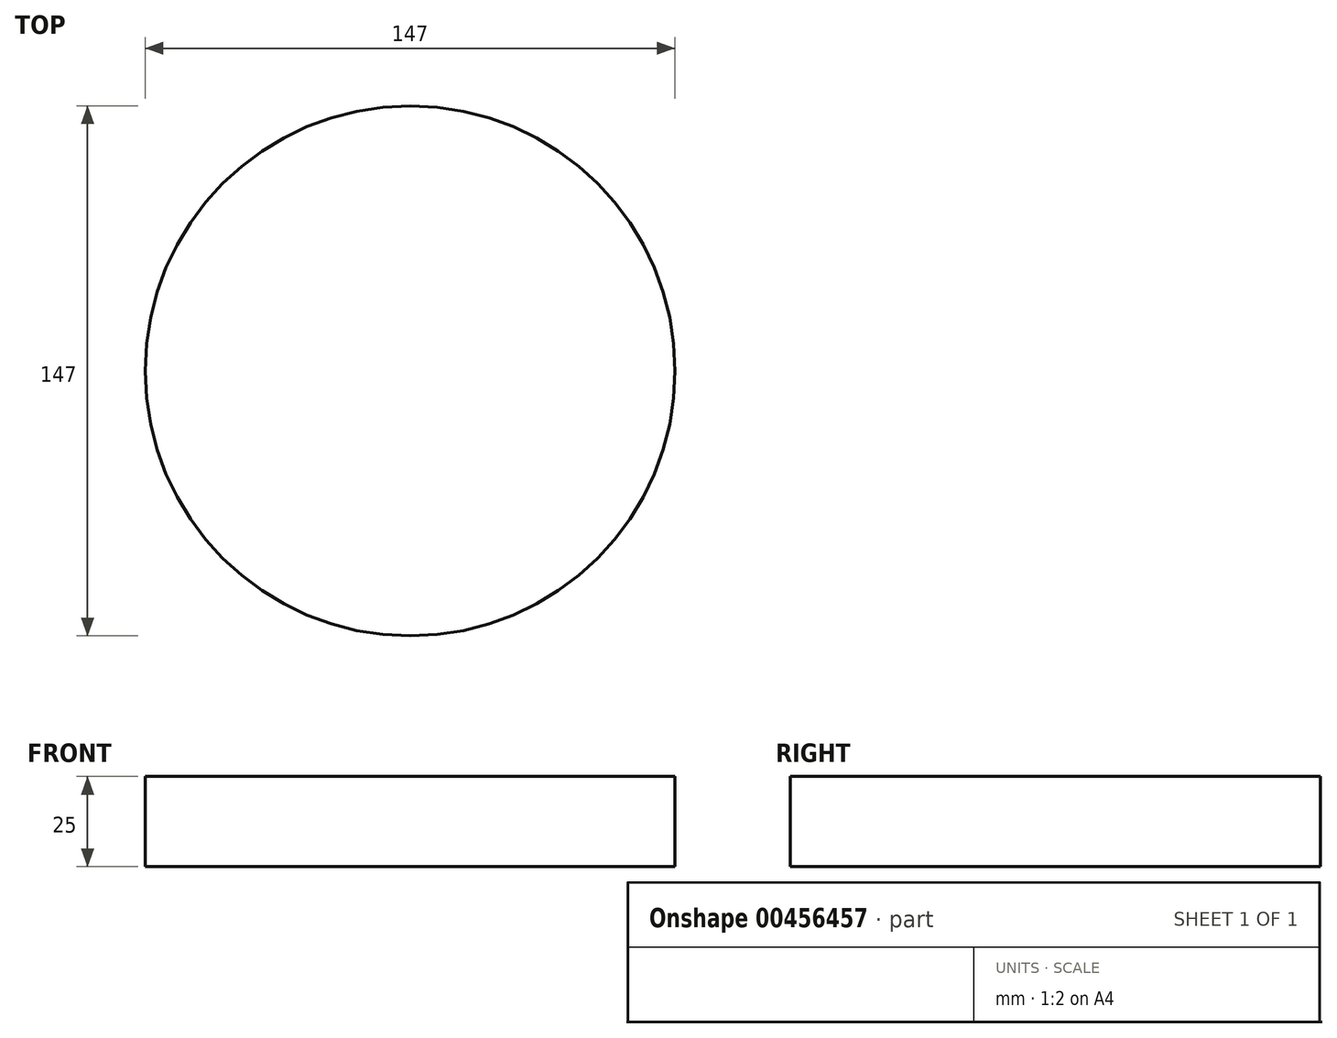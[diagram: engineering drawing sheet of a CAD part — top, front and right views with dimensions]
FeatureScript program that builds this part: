
annotation { "Feature Type Name" : "Feature", "Feature Type Description" : "" }
export const myFeature = defineFeature(function(context is Context, id is Id, definition is map)
    precondition{}
    {
        {
            var Q0;
            Q0=qCreatedBy(makeId("Top.planeOp"),FACE);
            var sketch = newSketch(context, id + "F0", { "sketchPlane" : qUnion([Q0])});
            skCircle(sketch, "E0", {"center": v(0, 0) * mm, "radius": 73.5 * mm});
            skSolve(sketch);
        }
        {
            var Q0;
            Q0=makeQuery(id+"F0.imprint","IMPRINT",FACE,{"disambiguationData":[TD([[makeQuery(id+"F0.imprint","IMPRINT",EDGE,{"derivedFrom":sQuery(id+"F0.wireOp",EDGE,"E0")}),1.0]])]});
            extrude(context, id + "F1", {"entities" : qUnion([Q0]), "depth" : 25 * mm});
        }
    });
